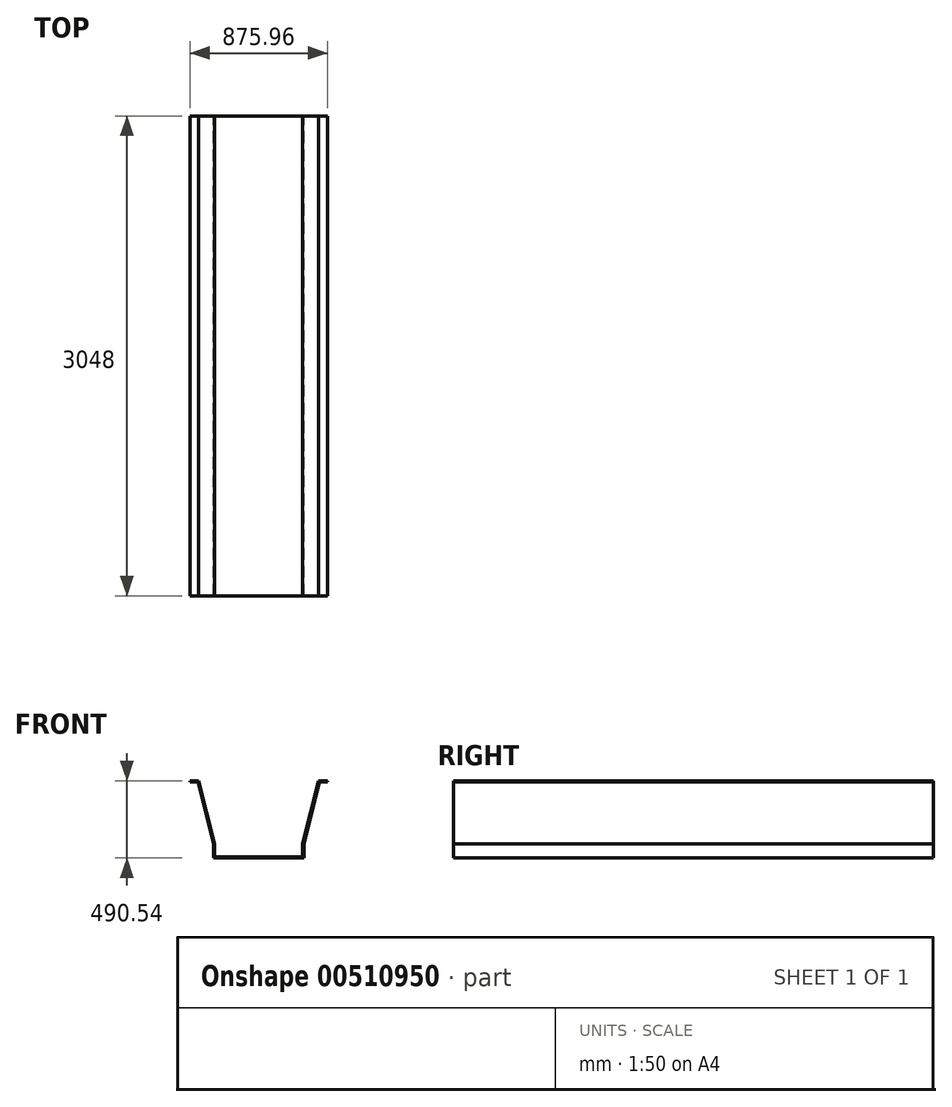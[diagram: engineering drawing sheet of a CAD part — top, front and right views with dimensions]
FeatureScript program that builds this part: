
annotation { "Feature Type Name" : "Feature", "Feature Type Description" : "" }
export const myFeature = defineFeature(function(context is Context, id is Id, definition is map)
    precondition{}
    {
        {
            var Q0;
            Q0=qCreatedBy(makeId("Front.planeOp"),FACE);
            var sketch = newSketch(context, id + "F0", { "sketchPlane" : qUnion([Q0])});
            skLineSegment(sketch, "E0", {"start": v(0, -210.2) * mm, "end": v(0, 763.05) * mm, "construction": true});
            skLineSegment(sketch, "E1", {"start": v(0, 0) * mm, "end": v(-287.34, 0) * mm});
            skLineSegment(sketch, "E2", {"start": v(-287.34, 0) * mm, "end": v(-287.34, 88.9) * mm});
            skLineSegment(sketch, "E3", {"start": v(-287.34, 88.9) * mm, "end": v(-387.18, 482.6) * mm});
            skLineSegment(sketch, "E4", {"start": v(-387.18, 482.6) * mm, "end": v(-437.98, 482.6) * mm});
            skLineSegment(sketch, "E5.MirrorCS", {"start": v(0, 0) * mm, "end": v(287.34, 0) * mm});
            skLineSegment(sketch, "E6.MirrorCS", {"start": v(287.34, 0) * mm, "end": v(287.34, 88.9) * mm});
            skLineSegment(sketch, "E7.MirrorCS", {"start": v(287.34, 88.9) * mm, "end": v(387.18, 482.6) * mm});
            skLineSegment(sketch, "E8.MirrorCS", {"start": v(387.18, 482.6) * mm, "end": v(437.98, 482.6) * mm});
            skLineSegment(sketch, "E9.0", {"start": v(-381, 490.54) * mm, "end": v(-437.98, 490.54) * mm});
            skLineSegment(sketch, "E9.1", {"start": v(-279.4, 89.9) * mm, "end": v(-381, 490.54) * mm});
            skLineSegment(sketch, "E9.2", {"start": v(-279.4, 7.94) * mm, "end": v(-279.4, 89.9) * mm});
            skLineSegment(sketch, "E9.3", {"start": v(0, 7.94) * mm, "end": v(-279.4, 7.94) * mm});
            skLineSegment(sketch, "E9.4", {"start": v(381, 490.54) * mm, "end": v(437.98, 490.54) * mm});
            skLineSegment(sketch, "E9.5", {"start": v(279.4, 89.9) * mm, "end": v(381, 490.54) * mm});
            skLineSegment(sketch, "E9.6", {"start": v(279.4, 7.94) * mm, "end": v(279.4, 89.9) * mm});
            skLineSegment(sketch, "E9.7", {"start": v(0, 7.94) * mm, "end": v(279.4, 7.94) * mm});
            skLineSegment(sketch, "E10", {"start": v(437.98, 490.54) * mm, "end": v(437.98, 482.6) * mm});
            skLineSegment(sketch, "E11", {"start": v(-437.98, 490.54) * mm, "end": v(-437.98, 482.6) * mm});
            skSolve(sketch);
        }
        {
            var Q0;
            Q0 = qSketchRegion(id + "F0", true);
            extrude(context, id + "F1", {"entities" : qUnion([Q0]), "depth" : 3048 * mm});
        }
    });
